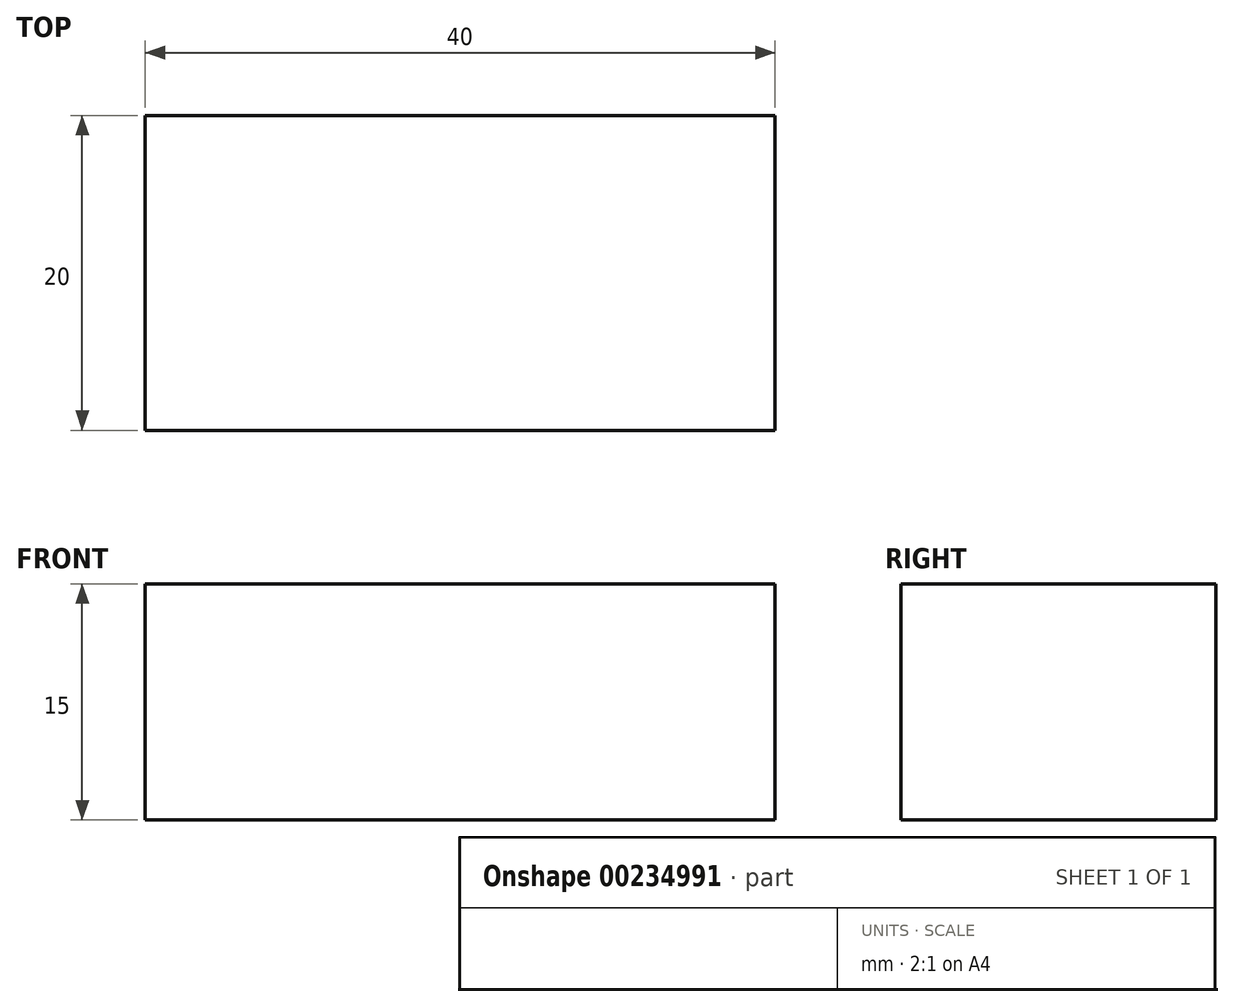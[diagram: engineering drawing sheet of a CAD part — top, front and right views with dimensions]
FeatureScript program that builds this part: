
annotation { "Feature Type Name" : "Feature", "Feature Type Description" : "" }
export const myFeature = defineFeature(function(context is Context, id is Id, definition is map)
    precondition{}
    {
        {
            var Q0;
            Q0=qCreatedBy(makeId("Front.planeOp"),FACE);
            var sketch = newSketch(context, id + "F0", { "sketchPlane" : qUnion([Q0])});
            skLineSegment(sketch, "E0.bottom", {"start": v(20, -7.5) * mm, "end": v(-20, -7.5) * mm});
            skLineSegment(sketch, "E0.top", {"start": v(20, 7.5) * mm, "end": v(-20, 7.5) * mm});
            skLineSegment(sketch, "E0.left", {"start": v(20, -7.5) * mm, "end": v(20, 7.5) * mm});
            skLineSegment(sketch, "E0.right", {"start": v(-20, -7.5) * mm, "end": v(-20, 7.5) * mm});
            skPoint(sketch, "E0.middle", {"position": v(0, 0) * mm});
            skSolve(sketch);
        }
        {
            var Q0;
            Q0=qSketchRegion(id+"F0",true);
            extrude(context, id + "F1", {"entities" : qUnion([Q0]), "endBound" : BoundingType.SYMMETRIC, "depth" : 20 * mm});
        }
    });
